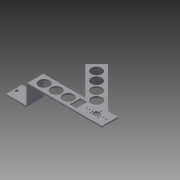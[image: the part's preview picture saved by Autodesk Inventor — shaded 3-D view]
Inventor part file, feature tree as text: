
AUTODESK INVENTOR PART (.ipt)
format: ipt  version: 2013 (Build 170138000, 138)  size: 385,536 bytes
history: native  units: in
note: dims shown in document units (in); Inventor stores cm internally (conversion verified against a paired STEP export)
features: sheet_metal_op x7, other x7, sketch x6
ambient origin geometry x8: Origin, YZ Plane, XZ Plane, XY Plane, X Axis, Y Axis, Z Axis, Center Point
bodies: Solid1 (feature_tree)
feature tree (20):
  sheet_metal_op  "Face1"
  sheet_metal_op  "Flange3"
  sheet_metal_op  "Flange4"
  sketch  "Sketch1"  dims[d5=3.0in]
  other  "Plate1"
  sketch  "Sketch4"  dims[d7=0.75in]
  other  "Plate4"
  sheet_metal_op  "Bend3"
  sheet_metal_op  "Corner3"
  sketch  "Sketch5"  dims[d8=0.125in]
  other  "Plate5"
  sheet_metal_op  "Bend4"
  sheet_metal_op  "Corner4"
  sketch  "Sketch6"  dims[d34=1.5in]
  sketch  "Sketch7"  dims[d35=1.5in]
  sketch  "Sketch8"  dims[d36=0.75in d37=0.75in d39=45.0deg d41=4.0in d42=4.0in d43=0.75in d44=1.25in d45=0.125in d46=0.0625in d47=0.25in d48=0.125in d49=2.0in d50=90.0deg d51=0.05in d52=0.5in d53=0.125in d54=0.125in d55=0.125in d56=0.0625in d57=0.25in d58=0.125in d59=2.0in d60=90.0deg d61=0.05in d62=0.5in d63=0.125in d64=0.125in d65=0.266in d66=0.266in d67=0.25in d68=0.75in d69=0.75in d70=0.25in d71=0.125in d72=0.0in d73=0.266in d74=0.266in d75=0.25in d76=0.75in d77=0.75in d78=0.25in d79=0.125in d80=0.0in d81=1.0in d82=1.0in d83=0.75in d84=0.75in d85=0.75in d86=0.75in d87=1.5748in d89=1.125in d90=0.3937in d92=1.0in d94=1.1811in d96=1.125in d97=0.3937in d99=1.0in d101=0.625in d102=0.625in d103=1.0in d104=0.25in d105=0.125in d106=0.0in d0=1.907in d1=0.125in d2=0.0625in d3=0.25in d4=0.125in d6=0.125in d9=0.125in d10=1.815in d11=0.125in d12=0.0625in d13=0.25in d14=0.125in d15=1.815in d16=0.125in d17=0.0625in d18=0.25in d19=0.125in d20=1.907in d21=0.125in d22=0.0625in d23=0.25in d24=0.125in d26=0.0625in d29=1.815in d30=0.0625in d31=0.25in d32=0.125in d33=0.125in d38=0.125in d40=0.0in]
  other  "Cut1"
  other  "Cut2"
  other  "Cut3"
  other  "Definition1"
